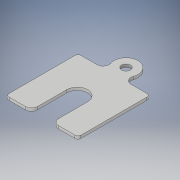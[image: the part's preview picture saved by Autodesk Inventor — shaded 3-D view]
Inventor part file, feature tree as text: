
AUTODESK INVENTOR PART (.ipt)
format: ipt  version: 2018 (Build 220112000, 112)  size: 140,288 bytes
history: native  units: in
note: dims shown in document units (in); Inventor stores cm internally (conversion verified against a paired STEP export)
features: extrude x1, sketch x1, fillet x1
ambient origin geometry x8: Origin, YZ Plane, XZ Plane, XY Plane, X Axis, Y Axis, Z Axis, Center Point
bodies: Solid1 (feature_tree)
feature tree (3):
  extrude  "Extrusion1"  Depth=1.0in TaperAngle=0.0deg
  sketch  "Sketch1"  dims[d0=0.183in d1=1.0in d2=0.0in]
  fillet  "Fillet2"  [1 undecoded]
note: 1 required parameter value undecoded (feature->parameter linkage not recoverable at this tier; creation-order binding heuristic only, values carry confidence <= 0.55)
